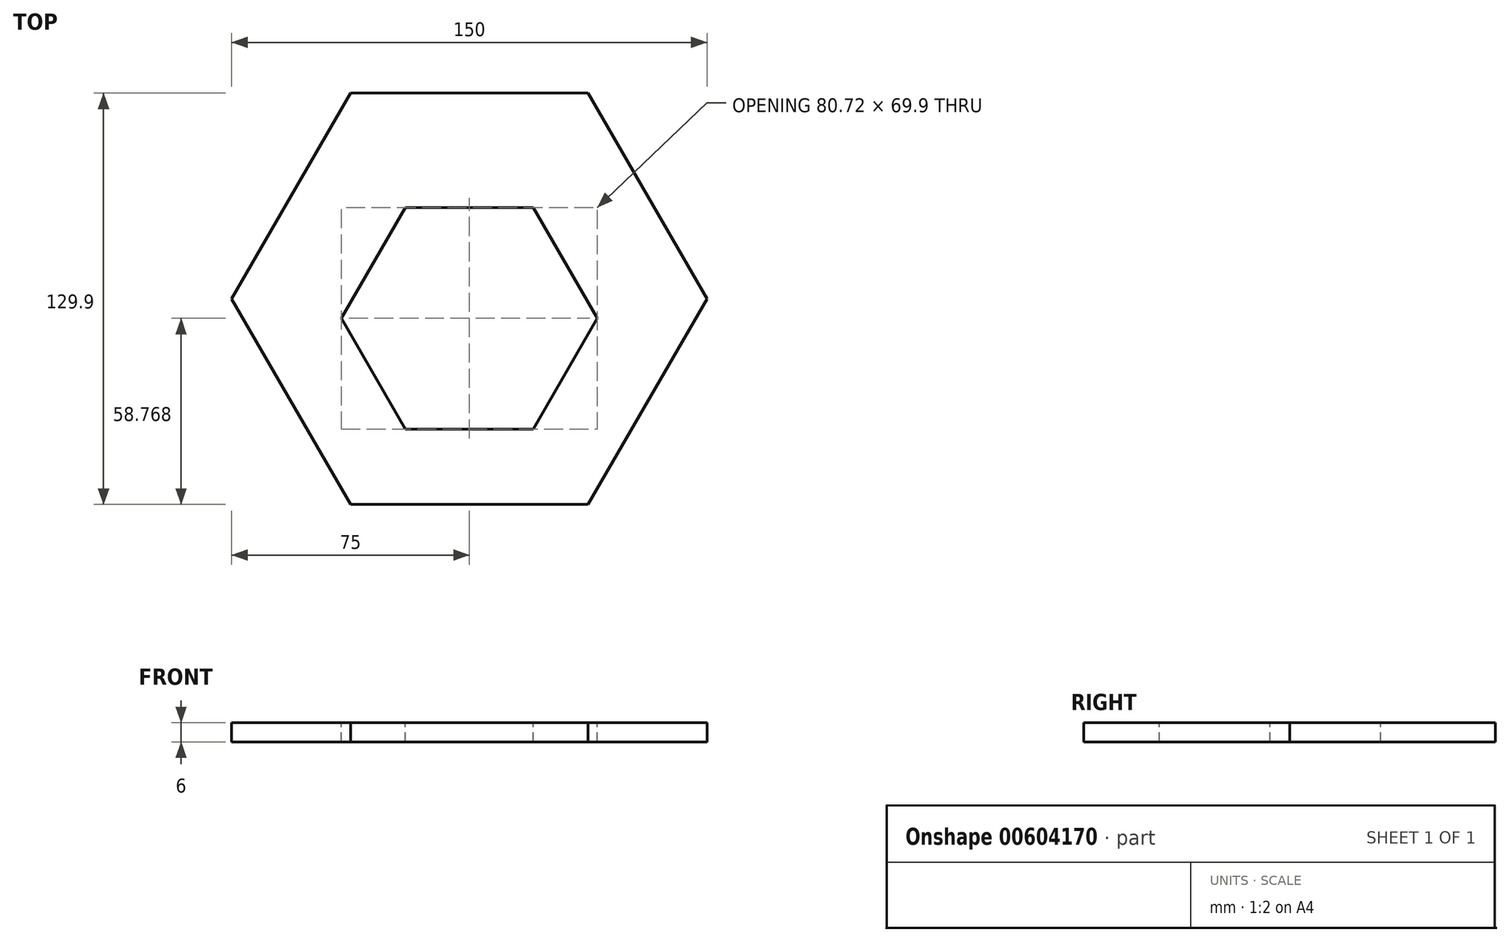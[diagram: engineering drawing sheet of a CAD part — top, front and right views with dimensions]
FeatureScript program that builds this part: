
annotation { "Feature Type Name" : "Feature", "Feature Type Description" : "" }
export const myFeature = defineFeature(function(context is Context, id is Id, definition is map)
    precondition{}
    {
        {
            var Q0;
            Q0=qCreatedBy(makeId("Top.planeOp"),FACE);
            var sketch = newSketch(context, id + "F0", { "sketchPlane" : qUnion([Q0])});
            skCircle(sketch, "E0.cCircle", {"center": v(0, 0) * mm, "radius": 64.95 * mm, "construction": true});
            skLineSegment(sketch, "E0.0", {"start": v(37.5, 64.95) * mm, "end": v(75, 0) * mm});
            skLineSegment(sketch, "E0.1", {"start": v(75, 0) * mm, "end": v(37.5, -64.95) * mm});
            skLineSegment(sketch, "E0.2", {"start": v(37.5, -64.95) * mm, "end": v(-37.5, -64.95) * mm});
            skLineSegment(sketch, "E0.3", {"start": v(-37.5, -64.95) * mm, "end": v(-75, 0) * mm});
            skLineSegment(sketch, "E0.4", {"start": v(-75, 0) * mm, "end": v(-37.5, 64.95) * mm});
            skLineSegment(sketch, "E0.5", {"start": v(-37.5, 64.95) * mm, "end": v(37.5, 64.95) * mm});
            skPoint(sketch, "E0.0.midPoint", {"position": v(64.95, 0) * mm});
            skSolve(sketch);
        }
        {
            var Q0;
            Q0 = qSketchRegion(id + "F0", true);
            extrude(context, id + "F1", {"entities" : qUnion([Q0]), "depth" : 6 * mm, "offsetDistance" : 25 * mm});
        }
        {
            var Q0;
            Q0=makeQuery(id+"F1.opExtrude","CAP_FACE",FACE,{"disambiguationData":[OSD([sQuery(id+"F0.wireOp",EDGE,"E0.0"),sQuery(id+"F0.wireOp",EDGE,"E0.1"),sQuery(id+"F0.wireOp",EDGE,"E0.2"),sQuery(id+"F0.wireOp",EDGE,"E0.3"),sQuery(id+"F0.wireOp",EDGE,"E0.4"),sQuery(id+"F0.wireOp",EDGE,"E0.5")])],"isStart":false});
            var sketch = newSketch(context, id + "F2", { "sketchPlane" : qUnion([Q0])});
            skCircle(sketch, "E1.cCircle", {"center": v(0, -6.18) * mm, "radius": 34.95 * mm, "construction": true});
            skLineSegment(sketch, "E1.0", {"start": v(20.18, 28.77) * mm, "end": v(40.36, -6.18) * mm});
            skLineSegment(sketch, "E1.1", {"start": v(40.36, -6.18) * mm, "end": v(20.18, -41.13) * mm});
            skLineSegment(sketch, "E1.2", {"start": v(20.18, -41.13) * mm, "end": v(-20.18, -41.13) * mm});
            skLineSegment(sketch, "E1.3", {"start": v(-20.18, -41.13) * mm, "end": v(-40.36, -6.18) * mm});
            skLineSegment(sketch, "E1.4", {"start": v(-40.36, -6.18) * mm, "end": v(-20.18, 28.77) * mm});
            skLineSegment(sketch, "E1.5", {"start": v(-20.18, 28.77) * mm, "end": v(20.18, 28.77) * mm});
            skPoint(sketch, "E1.0.midPoint", {"position": v(30.27, 11.3) * mm});
            skSolve(sketch);
        }
        {
            var Q0;
            Q0 = qSketchRegion(id + "F2", true);
            var Q1;
            Q1=makeQuery(id+"F1.opExtrude","CAP_FACE",FACE,{"disambiguationData":[OSD([sQuery(id+"F0.wireOp",EDGE,"E0.0"),sQuery(id+"F0.wireOp",EDGE,"E0.1"),sQuery(id+"F0.wireOp",EDGE,"E0.2"),sQuery(id+"F0.wireOp",EDGE,"E0.3"),sQuery(id+"F0.wireOp",EDGE,"E0.4"),sQuery(id+"F0.wireOp",EDGE,"E0.5")])],"isStart":true});
            extrude(context, id + "F3", {"entities" : qUnion([Q0]), "operationType" : NewBodyOperationType.REMOVE, "endBound" : BoundingType.UP_TO_SURFACE, "oppositeDirection" : true, "depth" : 25 * mm, "endBoundEntityFace" : qUnion([Q1]), "offsetDistance" : 25 * mm});
        }
    });
